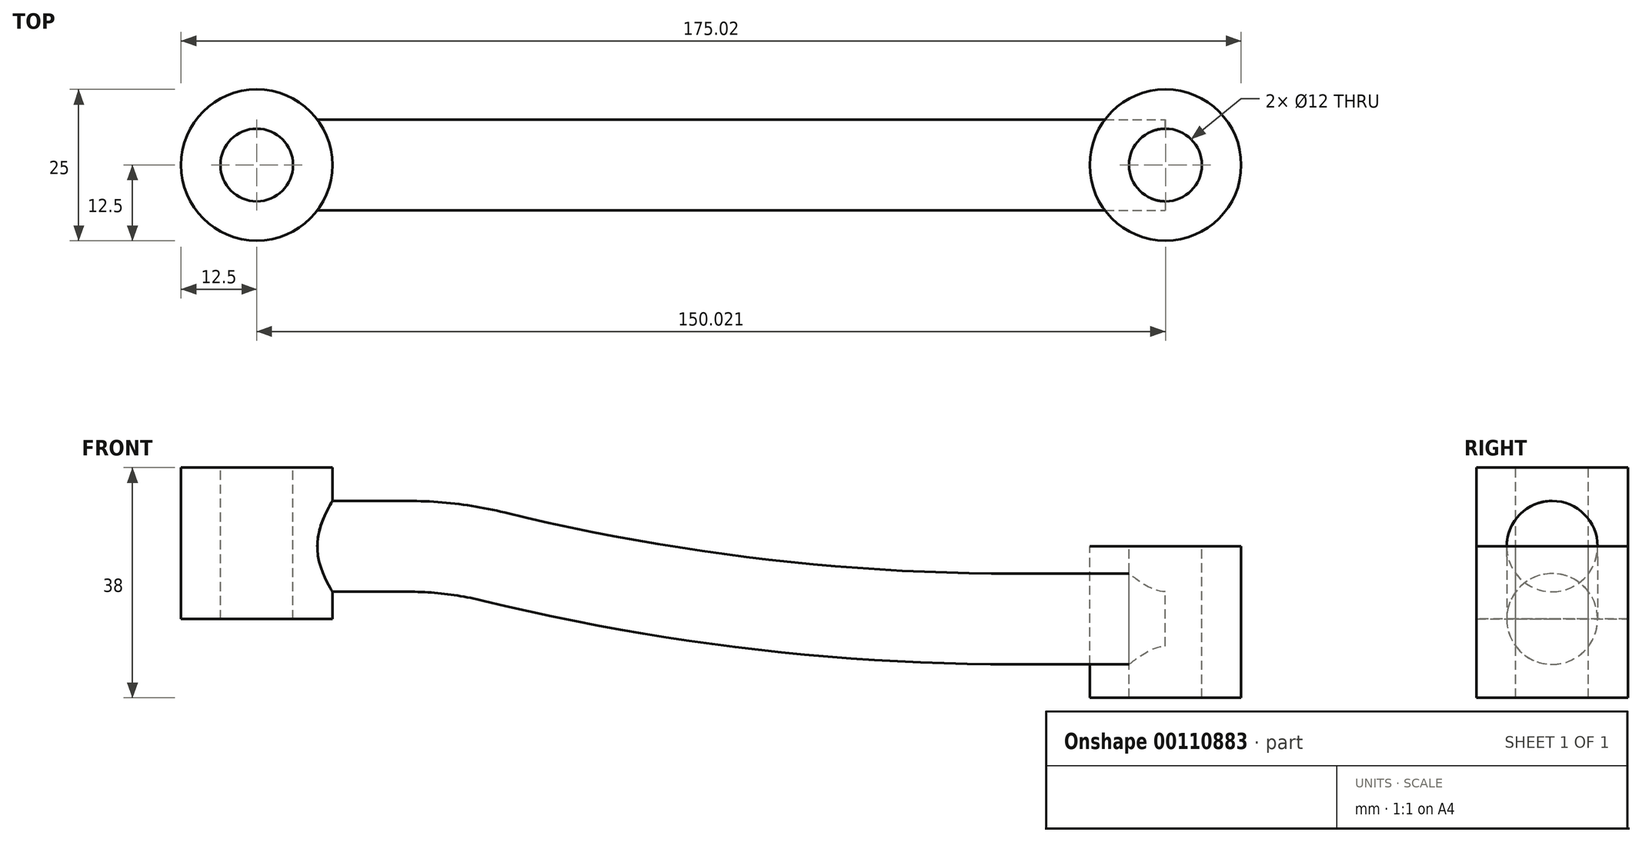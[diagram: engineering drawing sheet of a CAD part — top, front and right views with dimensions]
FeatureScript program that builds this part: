
annotation { "Feature Type Name" : "Feature", "Feature Type Description" : "" }
export const myFeature = defineFeature(function(context is Context, id is Id, definition is map)
    precondition{}
    {
        {
            var Q0;
            Q0=qCreatedBy(makeId("Front.planeOp"),FACE);
            var sketch = newSketch(context, id + "F0", { "sketchPlane" : qUnion([Q0])});
            skLineSegment(sketch, "E0", {"start": v(0, 0) * mm, "end": v(25, 0) * mm});
            skLineSegment(sketch, "E1", {"start": v(25, 14.16) * mm, "end": v(25, -12) * mm, "construction": true});
            skLineSegment(sketch, "E2", {"start": v(0, 14.16) * mm, "end": v(0, -12) * mm, "construction": true});
            skLineSegment(sketch, "E3", {"start": v(0, -12) * mm, "end": v(150, -12) * mm, "construction": true});
            skLineSegment(sketch, "E4", {"start": v(150, -12) * mm, "end": v(125, -12) * mm, "construction": true});
            skArc(sketch, "E5", {"start": v(25, 0) * mm, "mid": v(32.15, -0.43) * mm, "end": v(39.2, -1.7) * mm});
            skArc(sketch, "E6", {"start": v(39.2, -1.7) * mm, "mid": v(81.79, -9.42) * mm, "end": v(125, -12) * mm});
            skLineSegment(sketch, "E7", {"start": v(125, -12) * mm, "end": v(150, -12) * mm});
            skSolve(sketch);
        }
        {
            var Q0;
            Q0=qCreatedBy(makeId("Right.planeOp"),FACE);
            var sketch = newSketch(context, id + "F1", { "sketchPlane" : qUnion([Q0])});
            skCircle(sketch, "E8", {"center": v(0, 0) * mm, "radius": 7.5 * mm});
            skSolve(sketch);
        }
        {
            var Q0;
            Q0 = qSketchRegion(id + "F1", true);
            var Q1;
            Q1 = qConstructionFilter(qBodyType(qCreatedBy(id + "F0" ,EDGE), BodyType.WIRE), ConstructionObject.NO);
            sweep(context, id + "F2", {"profiles" : qUnion([Q0]), "path" : qUnion([Q1])});
        }
        {
            var Q0;
            Q0=qCreatedBy(makeId("Top.planeOp"),FACE);
            var sketch = newSketch(context, id + "F3", { "sketchPlane" : qUnion([Q0])});
            skCircle(sketch, "E9", {"center": v(0, 0) * mm, "radius": 12.5 * mm});
            skSolve(sketch);
        }
        {
            var Q0;
            Q0=makeQuery(id+"F3.imprint","IMPRINT",FACE,{"disambiguationData":[TD([[makeQuery(id+"F3.imprint","IMPRINT",EDGE,{"derivedFrom":sQuery(id+"F3.wireOp",EDGE,"E9")}),1.0]])]});
            extrude(context, id + "F4", {"entities" : qUnion([Q0]), "operationType" : NewBodyOperationType.ADD, "depth" : 13 * mm, "hasSecondDirection" : true, "secondDirectionOppositeDirection" : true, "secondDirectionDepth" : 12 * mm});
        }
        {
            var Q0;
            Q0=makeQuery(id+"F4.opExtrude","CAP_FACE",FACE,{"disambiguationData":[OSD([sQuery(id+"F3.wireOp",EDGE,"E9")])],"isStart":false});
            var sketch = newSketch(context, id + "F5", { "sketchPlane" : qUnion([Q0])});
            skCircle(sketch, "E10", {"center": v(0, 0) * mm, "radius": 6 * mm});
            skSolve(sketch);
        }
        {
            var Q0;
            Q0=makeQuery(id+"F5.imprint","IMPRINT",FACE,{"disambiguationData":[TD([[makeQuery(id+"F5.imprint","IMPRINT",EDGE,{"derivedFrom":sQuery(id+"F5.wireOp",EDGE,"E10")}),1.0]])]});
            extrude(context, id + "F6", {"entities" : qUnion([Q0]), "operationType" : NewBodyOperationType.REMOVE, "endBound" : BoundingType.THROUGH_ALL, "oppositeDirection" : true, "depth" : 25 * mm});
        }
        {
            var Q0;
            Q0=qCreatedBy(makeId("Top.planeOp"),FACE);
            var sketch = newSketch(context, id + "F7", { "sketchPlane" : qUnion([Q0])});
            skCircle(sketch, "E11", {"center": v(150.02, 0) * mm, "radius": 12.5 * mm});
            skPoint(sketch, "E12.0", {"position": v(150, 0) * mm});
            skSolve(sketch);
        }
        {
            var Q0;
            Q0=makeQuery(id+"F7.imprint","IMPRINT",FACE,{"disambiguationData":[TD([[makeQuery(id+"F7.imprint","IMPRINT",EDGE,{"derivedFrom":sQuery(id+"F7.wireOp",EDGE,"E11")}),1.0]])]});
            extrude(context, id + "F8", {"entities" : qUnion([Q0]), "oppositeDirection" : true, "depth" : 25 * mm});
        }
        {
            var Q0;
            Q0=makeQuery(id+"F8.opExtrude","CAP_FACE",FACE,{"disambiguationData":[OSD([sQuery(id+"F7.wireOp",EDGE,"E11")])],"isStart":true});
            var sketch = newSketch(context, id + "F9", { "sketchPlane" : qUnion([Q0])});
            skCircle(sketch, "E13", {"center": v(150.02, 0) * mm, "radius": 6 * mm});
            skSolve(sketch);
        }
        {
            var Q0;
            Q0=makeQuery(id+"F9.imprint","IMPRINT",FACE,{"disambiguationData":[TD([[makeQuery(id+"F9.imprint","IMPRINT",EDGE,{"derivedFrom":sQuery(id+"F9.wireOp",EDGE,"E13")}),1.0]])]});
            extrude(context, id + "F10", {"entities" : qUnion([Q0]), "operationType" : NewBodyOperationType.REMOVE, "endBound" : BoundingType.THROUGH_ALL, "oppositeDirection" : true, "depth" : 25 * mm});
        }
    });
